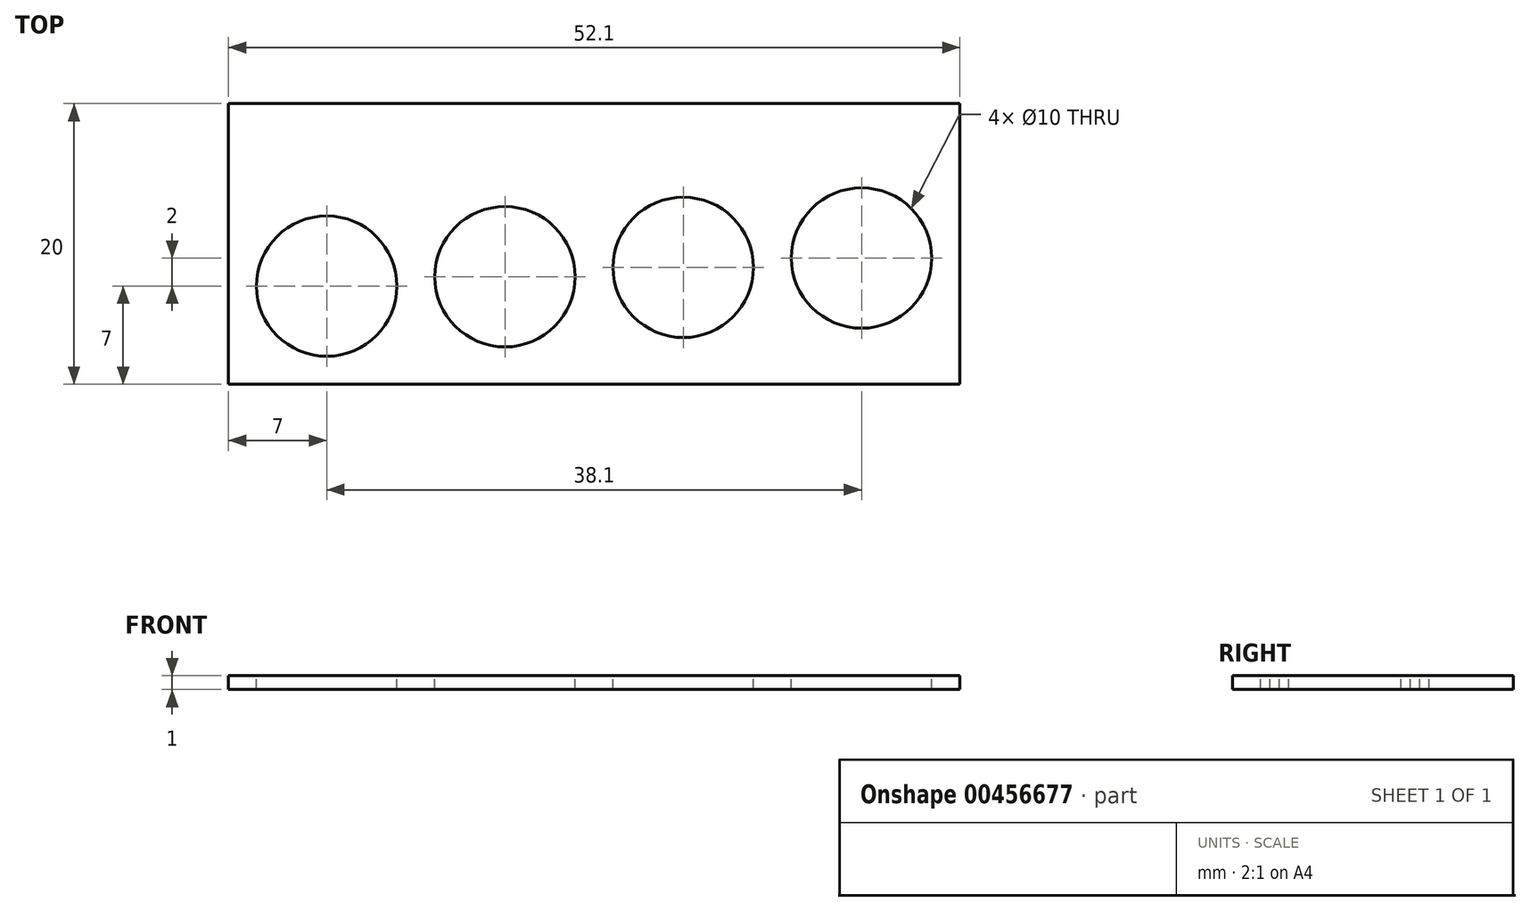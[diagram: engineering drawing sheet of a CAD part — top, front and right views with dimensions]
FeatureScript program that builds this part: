
annotation { "Feature Type Name" : "Feature", "Feature Type Description" : "" }
export const myFeature = defineFeature(function(context is Context, id is Id, definition is map)
    precondition{}
    {
        {
            var Q0;
            Q0=qCreatedBy(makeId("Top.planeOp"),FACE);
            var sketch = newSketch(context, id + "F0", { "sketchPlane" : qUnion([Q0])});
            skLineSegment(sketch, "E0.bottom", {"start": v(26.05, 10) * mm, "end": v(-26.05, 10) * mm});
            skLineSegment(sketch, "E0.top", {"start": v(26.05, -10) * mm, "end": v(-26.05, -10) * mm});
            skLineSegment(sketch, "E0.left", {"start": v(26.05, 10) * mm, "end": v(26.05, -10) * mm});
            skLineSegment(sketch, "E0.right", {"start": v(-26.05, 10) * mm, "end": v(-26.05, -10) * mm});
            skPoint(sketch, "E0.middle", {"position": v(0, 0) * mm});
            skLineSegment(sketch, "E1", {"start": v(19.05, 15.57) * mm, "end": v(19.05, -19.49) * mm, "construction": true});
            skLineSegment(sketch, "E2", {"start": v(6.35, 16.03) * mm, "end": v(6.35, -19.49) * mm, "construction": true});
            skLineSegment(sketch, "E3", {"start": v(-6.35, 15.57) * mm, "end": v(-6.35, -19.95) * mm, "construction": true});
            skLineSegment(sketch, "E4", {"start": v(-19.05, 16.03) * mm, "end": v(-19.05, -19.95) * mm, "construction": true});
            skCircle(sketch, "E5", {"center": v(-19.05, -3) * mm, "radius": 5 * mm});
            skCircle(sketch, "E6", {"center": v(19.05, -1) * mm, "radius": 5 * mm});
            skLineSegment(sketch, "E7", {"start": v(-19.05, -3) * mm, "end": v(19.05, -1) * mm, "construction": true});
            skCircle(sketch, "E8", {"center": v(6.35, -1.67) * mm, "radius": 5 * mm});
            skCircle(sketch, "E9", {"center": v(-6.35, -2.33) * mm, "radius": 5 * mm});
            skSolve(sketch);
        }
        {
            var Q0;
            Q0=makeQuery(id+"F0.imprint","IMPRINT",FACE,{"disambiguationData":[TD([[makeQuery(id+"F0.imprint","IMPRINT",EDGE,{"derivedFrom":sQuery(id+"F0.wireOp",EDGE,"E0.bottom")}),1.0]])]});
            extrude(context, id + "F1", {"entities" : qUnion([Q0]), "oppositeDirection" : true, "depth" : 1 * mm});
        }
    });
